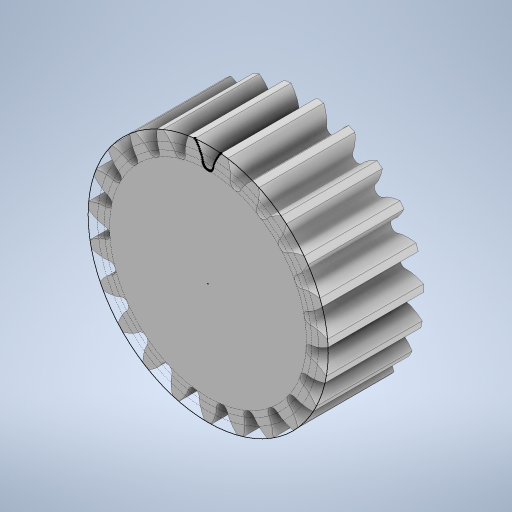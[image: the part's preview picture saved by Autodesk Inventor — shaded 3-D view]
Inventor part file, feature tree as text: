
AUTODESK INVENTOR PART (.ipt)
format: ipt  version: 2023.2 (Build 272271000, 271)  size: 382,976 bytes
history: native  units: mm
features: extrude x2, sketch x1, pattern_circular x1
ambient origin geometry x8: Origin, YZ Plane, XZ Plane, XY Plane, X Axis, Y Axis, Z Axis, Center Point
bodies: Solid1 (feature_tree)
feature tree (4):
  sketch  "Sketch1"  dims[d0=20.0mm d1=0.0mm d2=20.0mm d3=0.0mm d4=230.0mm d5=360.0deg]
  extrude  "Extrusion1"  TaperAngle=0.0deg  [1 undecoded]
  extrude  "Extrusion2"  Depth=20.0mm TaperAngle=0.0deg
  pattern_circular  "Circular Pattern1"  Count=23 Angle=360.0deg
note: 1 required parameter value undecoded (feature->parameter linkage not recoverable at this tier; creation-order binding heuristic only, values carry confidence <= 0.55)
